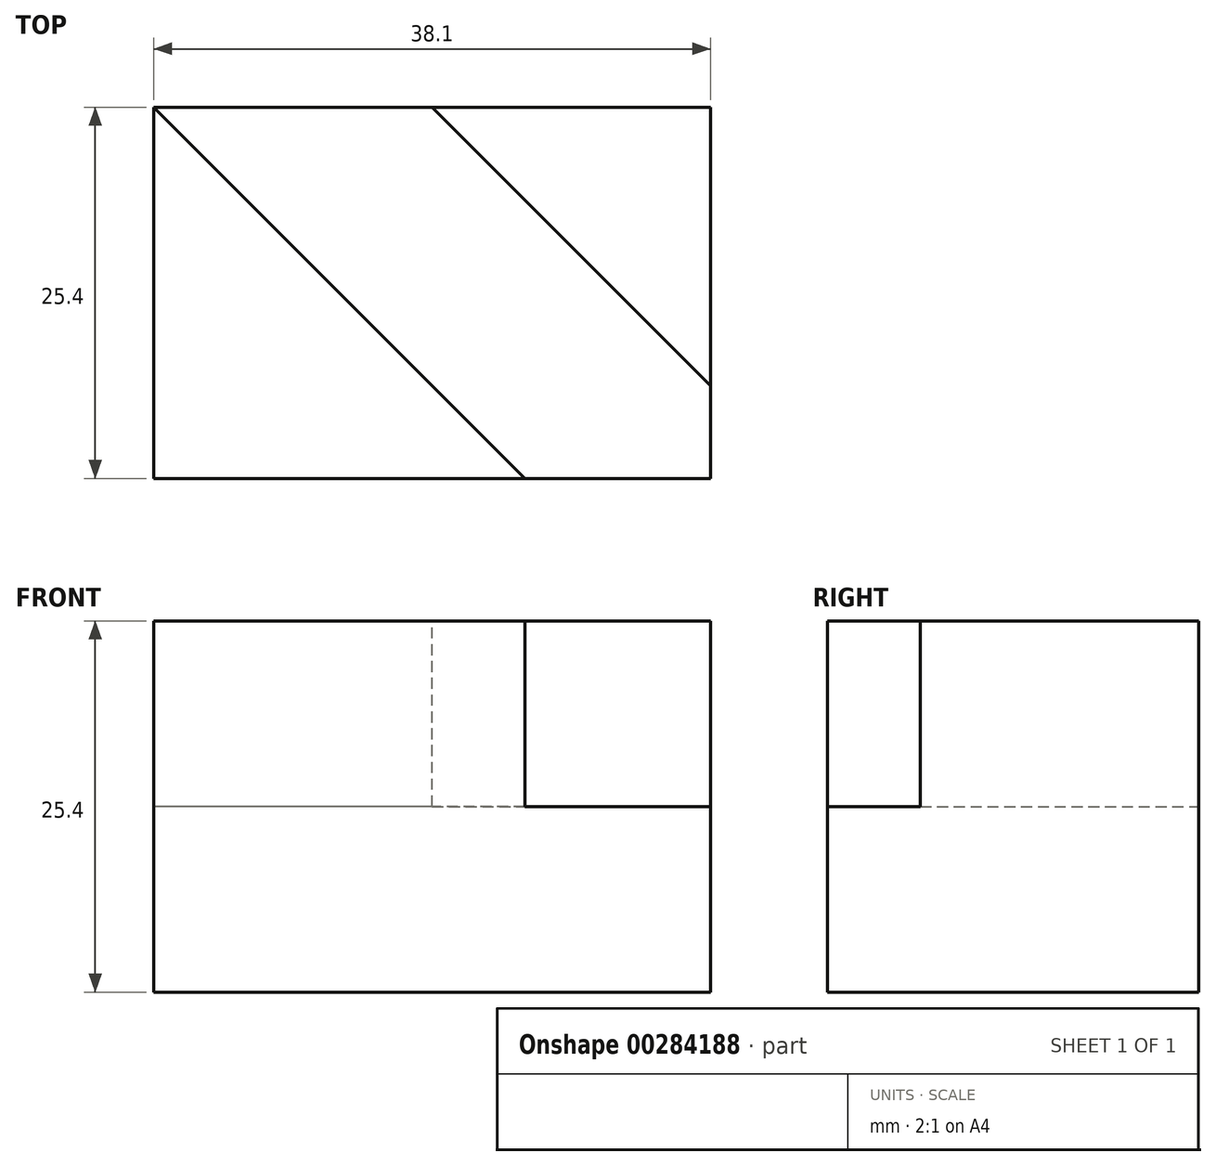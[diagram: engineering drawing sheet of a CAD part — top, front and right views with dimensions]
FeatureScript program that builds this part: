
annotation { "Feature Type Name" : "Feature", "Feature Type Description" : "" }
export const myFeature = defineFeature(function(context is Context, id is Id, definition is map)
    precondition{}
    {
        {
            var Q0;
            Q0=qCreatedBy(makeId("Right.planeOp"),FACE);
            var sketch = newSketch(context, id + "F0", { "sketchPlane" : qUnion([Q0])});
            skLineSegment(sketch, "E0.bottom", {"start": v(0, 0) * mm, "end": v(-25.4, 0) * mm});
            skLineSegment(sketch, "E0.top", {"start": v(0, 25.4) * mm, "end": v(-25.4, 25.4) * mm});
            skLineSegment(sketch, "E0.left", {"start": v(0, 0) * mm, "end": v(0, 25.4) * mm});
            skLineSegment(sketch, "E0.right", {"start": v(-25.4, 0) * mm, "end": v(-25.4, 25.4) * mm});
            skSolve(sketch);
        }
        {
            var Q0;
            Q0 = qSketchRegion(id + "F0", true);
            extrude(context, id + "F1", {"entities" : qUnion([Q0]), "depth" : 38.1 * mm});
        }
        {
            var Q0;
            Q0=makeQuery(id+"F1.opExtrude","SWEPT_FACE",FACE,{"disambiguationData":[OSD([sQuery(id+"F0.wireOp",EDGE,"E0.top")])]});
            var sketch = newSketch(context, id + "F2", { "sketchPlane" : qUnion([Q0])});
            skLineSegment(sketch, "E1", {"start": v(38.1, -25.4) * mm, "end": v(25.4, -25.4) * mm});
            skLineSegment(sketch, "E2", {"start": v(25.4, -25.4) * mm, "end": v(0, 0) * mm});
            skLineSegment(sketch, "E3", {"start": v(0, 0) * mm, "end": v(0, 0) * mm});
            skLineSegment(sketch, "E4", {"start": v(0, 0) * mm, "end": v(19.05, 0) * mm});
            skLineSegment(sketch, "E5", {"start": v(19.05, 0) * mm, "end": v(38.1, -19.05) * mm});
            skLineSegment(sketch, "E6", {"start": v(38.1, -19.05) * mm, "end": v(38.1, -25.4) * mm});
            skSolve(sketch);
        }
        {
            var Q0;
            Q0=makeQuery(id+"F2.imprint","IMPRINT",FACE,{"disambiguationData":[TD([[makeQuery(id+"F2.imprint","IMPRINT",EDGE,{"derivedFrom":sQuery(id+"F2.wireOp",EDGE,"E1")}),-1.0]])]});
            extrude(context, id + "F3", {"entities" : qUnion([Q0]), "operationType" : NewBodyOperationType.REMOVE, "oppositeDirection" : true, "depth" : 12.7 * mm});
        }
    });
